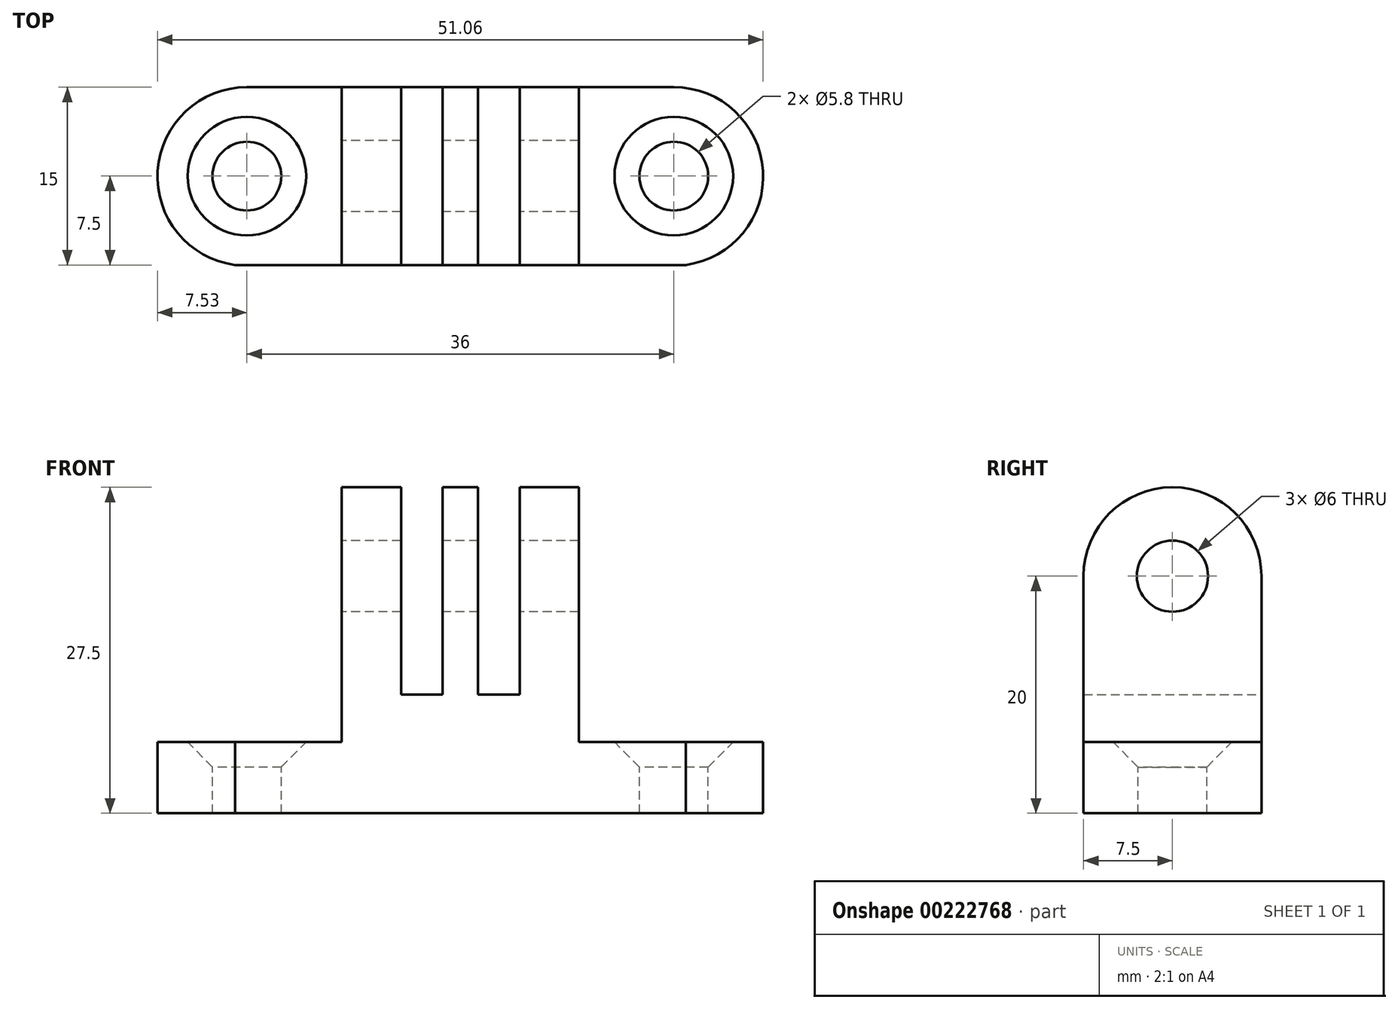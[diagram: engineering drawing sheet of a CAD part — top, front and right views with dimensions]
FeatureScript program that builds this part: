
annotation { "Feature Type Name" : "Feature", "Feature Type Description" : "" }
export const myFeature = defineFeature(function(context is Context, id is Id, definition is map)
    precondition{}
    {
        {
            var Q0;
            Q0=qCreatedBy(makeId("Right.planeOp"),FACE);
            var sketch = newSketch(context, id + "F0", { "sketchPlane" : qUnion([Q0])});
            skArc(sketch, "E0", {"start": v(7.5, 0) * mm, "mid": v(0, 7.5) * mm, "end": v(-7.5, 0) * mm});
            skCircle(sketch, "E1", {"center": v(0, 0) * mm, "radius": 3 * mm});
            skLineSegment(sketch, "E2.left", {"start": v(7.5, 0) * mm, "end": v(7.5, -20) * mm});
            skLineSegment(sketch, "E2.right", {"start": v(-7.5, 0) * mm, "end": v(-7.5, -20) * mm});
            skLineSegment(sketch, "E3", {"start": v(-7.5, -20) * mm, "end": v(7.5, -20) * mm});
            skSolve(sketch);
        }
        {
            var Q0;
            Q0=makeQuery(id+"F0.imprint","IMPRINT",FACE,{"disambiguationData":[TD([[makeQuery(id+"F0.imprint","IMPRINT",EDGE,{"derivedFrom":sQuery(id+"F0.wireOp",EDGE,"E0")}),1.0]])]});
            extrude(context, id + "F1", {"entities" : qUnion([Q0]), "depth" : 20 * mm});
        }
        {
            var Q0;
            Q0=qCreatedBy(makeId("Front.planeOp"),FACE);
            var sketch = newSketch(context, id + "F2", { "sketchPlane" : qUnion([Q0])});
            skLineSegment(sketch, "E4.bottom", {"start": v(8.5, 10) * mm, "end": v(5, 10) * mm});
            skLineSegment(sketch, "E4.top", {"start": v(8.5, -10) * mm, "end": v(5, -10) * mm});
            skLineSegment(sketch, "E4.left", {"start": v(8.5, 10) * mm, "end": v(8.5, -10) * mm});
            skLineSegment(sketch, "E4.right", {"start": v(5, 10) * mm, "end": v(5, -10) * mm});
            skPoint(sketch, "E4.middle", {"position": v(6.75, 0) * mm});
            skLineSegment(sketch, "E5.bottom", {"start": v(15, 10) * mm, "end": v(11.5, 10) * mm});
            skLineSegment(sketch, "E5.top", {"start": v(15, -10) * mm, "end": v(11.5, -10) * mm});
            skLineSegment(sketch, "E5.left", {"start": v(15, 10) * mm, "end": v(15, -10) * mm});
            skLineSegment(sketch, "E5.right", {"start": v(11.5, 10) * mm, "end": v(11.5, -10) * mm});
            skPoint(sketch, "E5.middle", {"position": v(13.25, 0) * mm});
            skSolve(sketch);
        }
        {
            var Q0;
            Q0 = qSketchRegion(id + "F2", true);
            extrude(context, id + "F3", {"entities" : qUnion([Q0]), "operationType" : NewBodyOperationType.REMOVE, "depth" : 25 * mm, "hasSecondDirection" : true, "secondDirectionOppositeDirection" : true, "secondDirectionDepth" : 10 * mm});
        }
        {
            var Q0;
            Q0=makeQuery(id+"F1.opExtrude","SWEPT_FACE",FACE,{"disambiguationData":[OSD([sQuery(id+"F0.wireOp",EDGE,"E3")])]});
            var sketch = newSketch(context, id + "F4", { "sketchPlane" : qUnion([Q0])});
            skLineSegment(sketch, "E6.bottom", {"start": v(20, -7.5) * mm, "end": v(28, -7.5) * mm});
            skLineSegment(sketch, "E6.top", {"start": v(20, 7.5) * mm, "end": v(29, 7.5) * mm});
            skLineSegment(sketch, "E6.left", {"start": v(20, -7.5) * mm, "end": v(20, 7.5) * mm});
            skLineSegment(sketch, "E7.bottom", {"start": v(0, -7.5) * mm, "end": v(-8, -7.5) * mm});
            skLineSegment(sketch, "E7.top", {"start": v(0, 7.5) * mm, "end": v(-9, 7.5) * mm});
            skLineSegment(sketch, "E7.left", {"start": v(0, -7.5) * mm, "end": v(0, 7.5) * mm});
            skArc(sketch, "E8", {"start": v(-8, -7.5) * mm, "mid": v(-15.52, -0.47) * mm, "end": v(-9, 7.5) * mm});
            skArc(sketch, "E9", {"start": v(28, -7.5) * mm, "mid": v(35.52, -0.47) * mm, "end": v(29, 7.5) * mm});
            skSolve(sketch);
        }
        {
            var Q0;
            Q0 = qSketchRegion(id + "F4", true);
            extrude(context, id + "F5", {"entities" : qUnion([Q0]), "operationType" : NewBodyOperationType.ADD, "oppositeDirection" : true, "depth" : 6 * mm});
        }
        {
            var Q0;
            Q0=makeQuery(id+"F5.opExtrude","CAP_FACE",FACE,{"disambiguationData":[OSD([sQuery(id+"F4.wireOp",EDGE,"E7.bottom"),sQuery(id+"F4.wireOp",EDGE,"E7.top"),sQuery(id+"F4.wireOp",EDGE,"E7.left"),sQuery(id+"F4.wireOp",EDGE,"E8")])],"isStart":false});
            var sketch = newSketch(context, id + "F6", { "sketchPlane" : qUnion([Q0])});
            skPoint(sketch, "E10", {"position": v(-8, 0) * mm});
            skPoint(sketch, "E11", {"position": v(28, 0) * mm});
            skSolve(sketch);
        }
        {
            var Q0;
            Q0=sQuery(id+"F6.wireOp",VERTEX,"E10");
            var Q1;
            Q1=sQuery(id+"F6.wireOp",VERTEX,"E11");
            var Q2;
            Q2=makeQuery(id+"F1.opExtrude","SWEPT_BODY",BODY,{"disambiguationData":[OSD([sQuery(id+"F0.wireOp",EDGE,"E0"),sQuery(id+"F0.wireOp",EDGE,"E1"),sQuery(id+"F0.wireOp",EDGE,"E2.left"),sQuery(id+"F0.wireOp",EDGE,"E2.right"),sQuery(id+"F0.wireOp",EDGE,"E3")])]});
            hole(context, id + "F7", {"style" : HoleStyle.C_SINK, "endStyle" : HoleEndStyle.THROUGH, "holeDiameter" : 5.8 * mm, "cSinkDiameter" : 10 * mm, "cSinkAngle" : 90 * degree, "locations" : qUnion([Q0, Q1]), "scope" : qUnion([Q2]), "isTappedThrough" : true});
        }
    });
